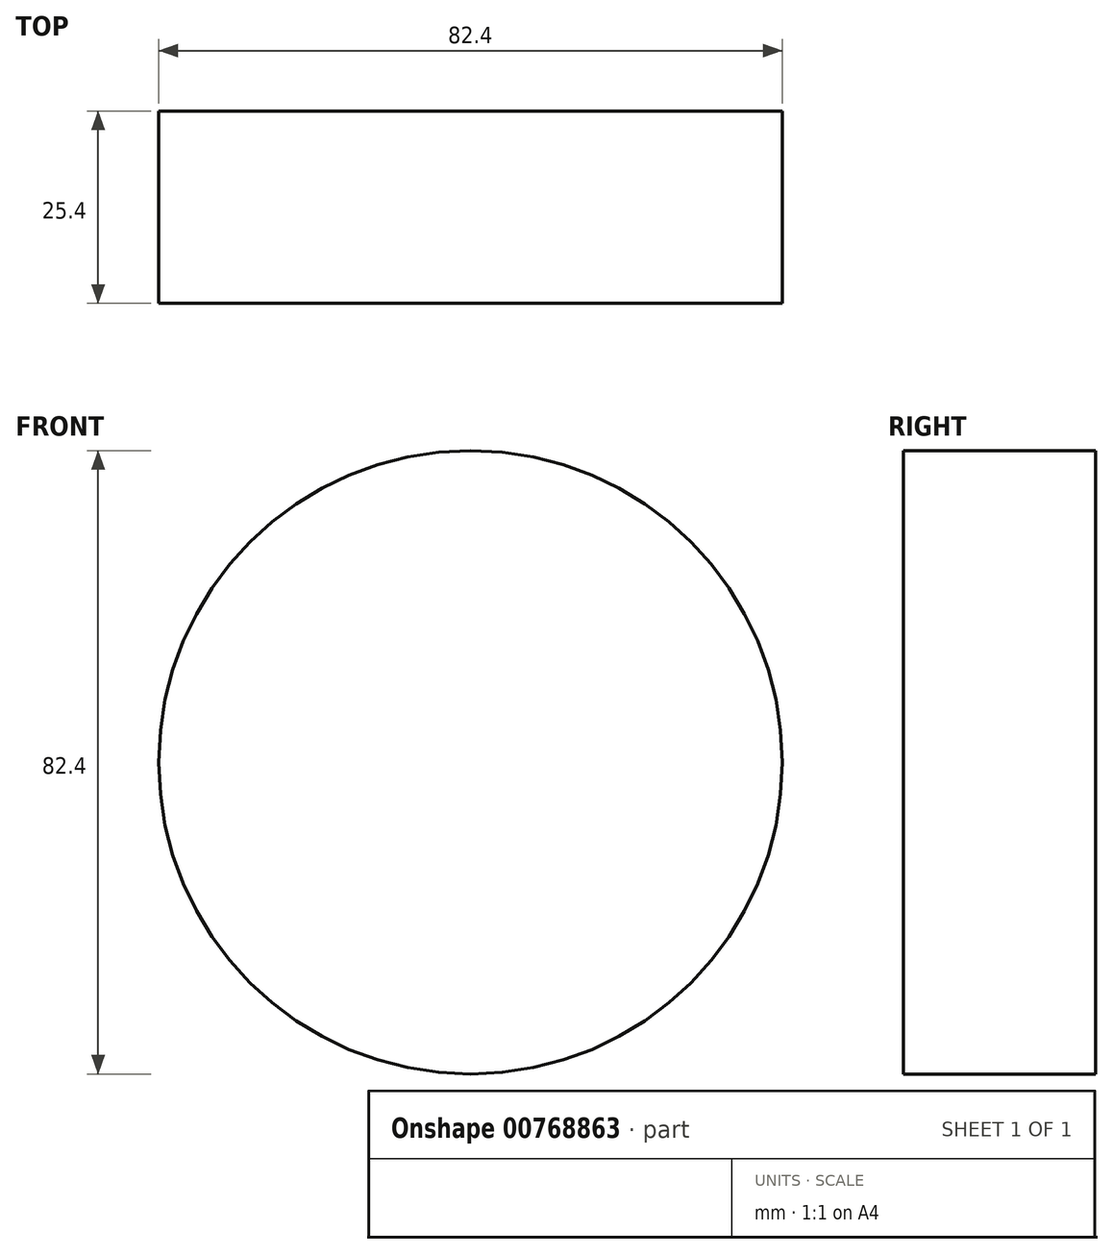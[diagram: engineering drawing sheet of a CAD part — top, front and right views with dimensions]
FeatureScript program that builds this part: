
annotation { "Feature Type Name" : "Feature", "Feature Type Description" : "" }
export const myFeature = defineFeature(function(context is Context, id is Id, definition is map)
    precondition{}
    {
        {
            var Q0;
            Q0=qCreatedBy(makeId("Front.planeOp"),FACE);
            var sketch = newSketch(context, id + "F0", { "sketchPlane" : qUnion([Q0])});
            skCircle(sketch, "E0", {"center": v(16.27, 37.85) * mm, "radius": 41.2 * mm});
            skPoint(sketch, "E0.first.point", {"position": v(0, 0) * mm});
            skPoint(sketch, "E0.second.point", {"position": v(57.26, 41.99) * mm});
            skPoint(sketch, "E0.third.point", {"position": v(21.44, -3.02) * mm});
            skSolve(sketch);
        }
        {
            var Q0;
            Q0=makeQuery(id+"F0.imprint","IMPRINT",FACE,{"disambiguationData":[TD([[makeQuery(id+"F0.imprint","IMPRINT",EDGE,{"derivedFrom":sQuery(id+"F0.wireOp",EDGE,"E0")}),1.0]])]});
            extrude(context, id + "F1", {"entities" : qUnion([Q0]), "depth" : 25.4 * mm, "offsetDistance" : 25.4 * mm});
        }
    });
